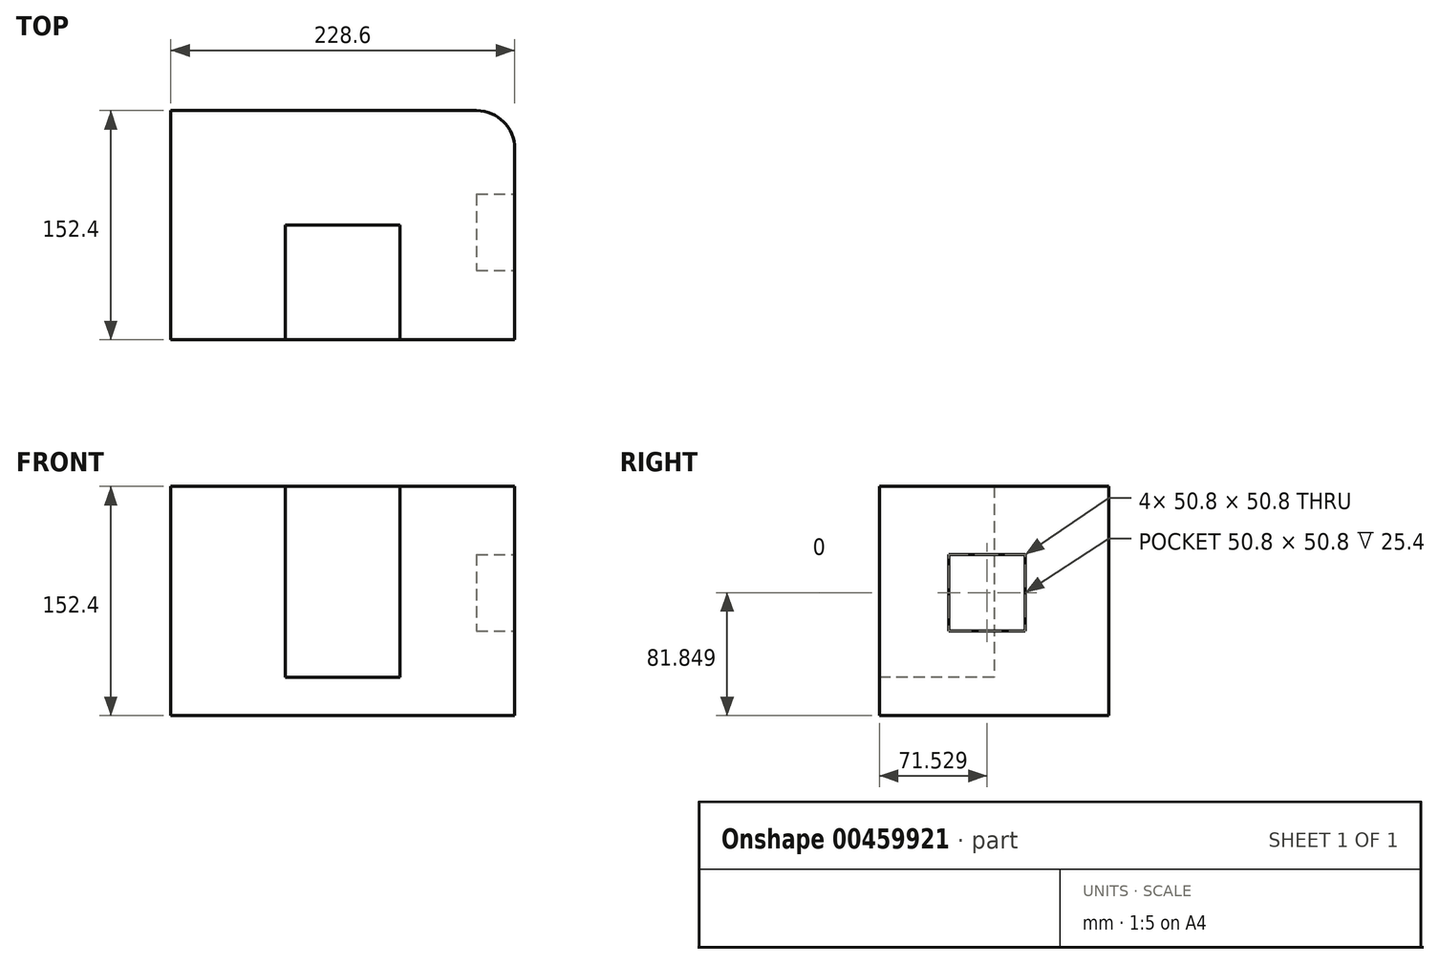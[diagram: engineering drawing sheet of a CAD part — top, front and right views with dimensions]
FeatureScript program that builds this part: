
annotation { "Feature Type Name" : "Feature", "Feature Type Description" : "" }
export const myFeature = defineFeature(function(context is Context, id is Id, definition is map)
    precondition{}
    {
        {
            var Q0;
            Q0=qCreatedBy(makeId("Front.planeOp"),FACE);
            var sketch = newSketch(context, id + "F0", { "sketchPlane" : qUnion([Q0])});
            skLineSegment(sketch, "E0", {"start": v(0, 0) * mm, "end": v(-228.6, 0) * mm});
            skLineSegment(sketch, "E1", {"start": v(-228.6, 0) * mm, "end": v(-228.6, 152.4) * mm});
            skLineSegment(sketch, "E2", {"start": v(-228.6, 152.4) * mm, "end": v(-161.75, 152.4) * mm});
            skLineSegment(sketch, "E3", {"start": v(-161.75, 152.4) * mm, "end": v(0, 152.4) * mm});
            skLineSegment(sketch, "E4", {"start": v(0, 152.4) * mm, "end": v(0, 0) * mm});
            skSolve(sketch);
        }
        {
            var Q0;
            Q0=makeQuery(id+"F0.imprint","IMPRINT",FACE,{"disambiguationData":[TD([[makeQuery(id+"F0.imprint","IMPRINT",EDGE,{"derivedFrom":sQuery(id+"F0.wireOp",EDGE,"E0")}),-1.0]])]});
            extrude(context, id + "F1", {"entities" : qUnion([Q0]), "depth" : 152.4 * mm});
        }
        {
            var Q0;
            Q0=makeQuery(id+"F1.opExtrude","CAP_FACE",FACE,{"disambiguationData":[OSD([sQuery(id+"F0.wireOp",EDGE,"E0"),sQuery(id+"F0.wireOp",EDGE,"E1"),sQuery(id+"F0.wireOp",EDGE,"E2"),sQuery(id+"F0.wireOp",EDGE,"E3"),sQuery(id+"F0.wireOp",EDGE,"E4")])],"isStart":false});
            var sketch = newSketch(context, id + "F2", { "sketchPlane" : qUnion([Q0])});
            skLineSegment(sketch, "E5", {"start": v(-152.4, 152.4) * mm, "end": v(-152.4, 25.4) * mm});
            skLineSegment(sketch, "E6", {"start": v(-152.4, 25.4) * mm, "end": v(-76.2, 25.4) * mm});
            skLineSegment(sketch, "E7", {"start": v(-76.2, 25.4) * mm, "end": v(-76.2, 152.4) * mm});
            skSolve(sketch);
        }
        {
            var Q0;
            Q0 = qSketchRegion(id + "F2", true);
            var Q1;
            {var subQ0=sQuery(id+"F2.wireOp",EDGE,"E5");Q1=makeQuery(id+"F2.imprint","IMPRINT",FACE,{"disambiguationData":[TD([[makeQuery(id+"F2.imprint","IMPRINT",EDGE,{"derivedFrom":subQ0}),1.0]])]});}
            extrude(context, id + "F3", {"entities" : qUnion([Q0, Q1]), "operationType" : NewBodyOperationType.REMOVE, "oppositeDirection" : true, "depth" : 76.2 * mm});
        }
        {
            var Q0;
            Q0=makeQuery(id+"F1.opExtrude","SWEPT_FACE",FACE,{"disambiguationData":[OSD([sQuery(id+"F0.wireOp",EDGE,"E4")])]});
            var sketch = newSketch(context, id + "F4", { "sketchPlane" : qUnion([Q0])});
            skLineSegment(sketch, "E8", {"start": v(-106.27, 107.25) * mm, "end": v(-106.27, 56.45) * mm});
            skLineSegment(sketch, "E9", {"start": v(-106.27, 56.45) * mm, "end": v(-55.47, 56.45) * mm});
            skLineSegment(sketch, "E10", {"start": v(-55.47, 56.45) * mm, "end": v(-55.47, 107.25) * mm});
            skLineSegment(sketch, "E11", {"start": v(-55.47, 107.25) * mm, "end": v(-106.27, 107.25) * mm});
            skSolve(sketch);
        }
        {
            var Q0;
            Q0=makeQuery(id+"F4.imprint","IMPRINT",FACE,{"disambiguationData":[TD([[makeQuery(id+"F4.imprint","IMPRINT",EDGE,{"derivedFrom":sQuery(id+"F4.wireOp",EDGE,"E8")}),1.0]])]});
            extrude(context, id + "F5", {"entities" : qUnion([Q0]), "operationType" : NewBodyOperationType.REMOVE, "oppositeDirection" : true, "depth" : 25.4 * mm});
        }
        {
            var Q0;
            Q0=makeQuery(id+"F1.opExtrude","CAP_EDGE",EDGE,{"disambiguationData":[OSD([sQuery(id+"F0.wireOp",EDGE,"E4")])],"isStart":true});
            fillet(context, id + "F6", {"entities" : qUnion([Q0]), "radius" : 25.4 * mm, "tangentPropagation" : true, "allowEdgeOverflow" : false});
        }
    });
